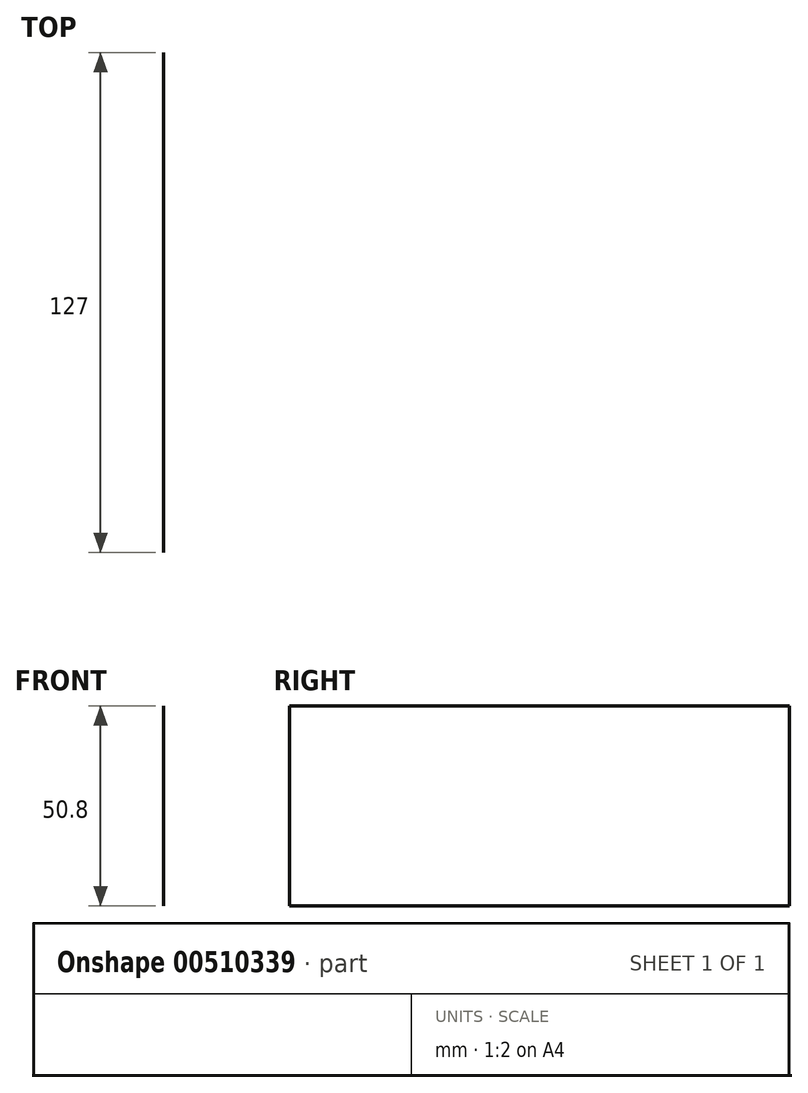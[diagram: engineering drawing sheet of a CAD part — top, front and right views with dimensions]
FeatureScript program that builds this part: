
annotation { "Feature Type Name" : "Feature", "Feature Type Description" : "" }
export const myFeature = defineFeature(function(context is Context, id is Id, definition is map)
    precondition{}
    {
        {
            var Q0;
            Q0=qCreatedBy(makeId("Front.planeOp"),FACE);
            var sketch = newSketch(context, id + "F0", { "sketchPlane" : qUnion([Q0])});
            skLineSegment(sketch, "E0", {"start": v(0, 0) * mm, "end": v(25.4, 0) * mm});
            skLineSegment(sketch, "E1", {"start": v(25.4, 0) * mm, "end": v(25.4, 50.8) * mm});
            skLineSegment(sketch, "E2", {"start": v(25.4, 50.8) * mm, "end": v(0, 50.8) * mm});
            skLineSegment(sketch, "E3", {"start": v(0, 50.8) * mm, "end": v(0, 0) * mm});
            skSolve(sketch);
        }
        {
            var Q0;
            Q0=makeQuery(id+"F0.imprint","IMPRINT",FACE,{"disambiguationData":[TD([[makeQuery(id+"F0.imprint","IMPRINT",EDGE,{"derivedFrom":sQuery(id+"F0.wireOp",EDGE,"E0")}),1.0]])]});
            var Q1;
            Q1=sQuery(id+"F0.wireOp",EDGE,"E1");
            extrude(context, id + "F1", {"entities" : qUnion([Q0]), "bodyType" : ToolBodyType.SURFACE, "surfaceEntities" : qUnion([Q1]), "depth" : 127 * mm});
        }
    });
